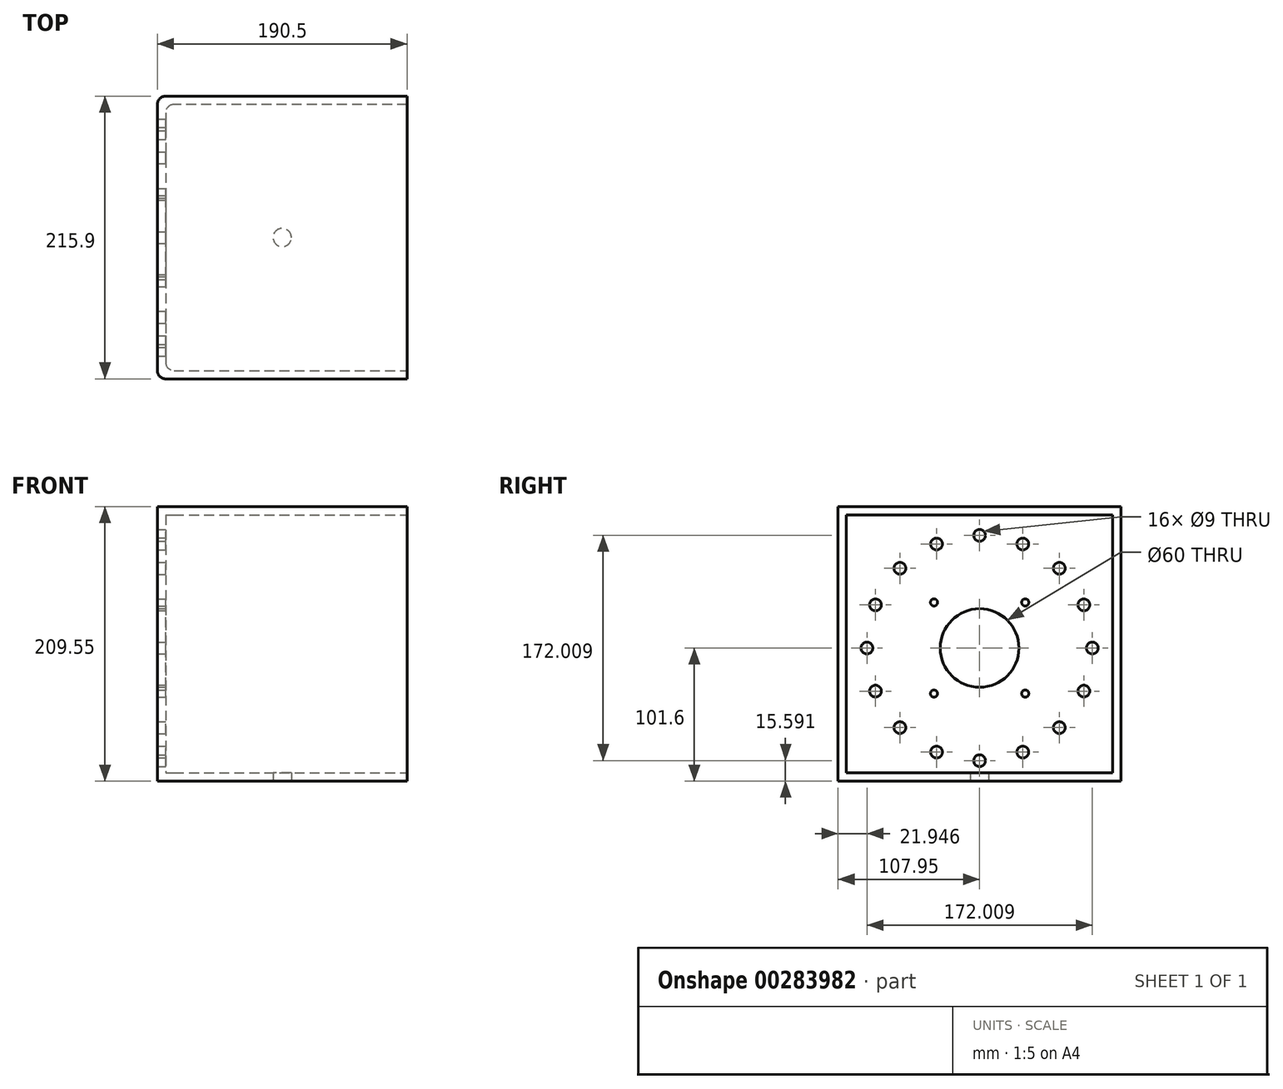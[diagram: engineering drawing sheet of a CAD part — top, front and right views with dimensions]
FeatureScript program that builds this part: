
annotation { "Feature Type Name" : "Feature", "Feature Type Description" : "" }
export const myFeature = defineFeature(function(context is Context, id is Id, definition is map)
    precondition{}
    {
        {
            var Q0;
            Q0=qCreatedBy(makeId("Top.planeOp"),FACE);
            var sketch = newSketch(context, id + "F0", { "sketchPlane" : qUnion([Q0])});
            skLineSegment(sketch, "E0.bottom", {"start": v(95.25, -107.95) * mm, "end": v(-88.9, -107.95) * mm});
            skLineSegment(sketch, "E0.top", {"start": v(95.25, 107.95) * mm, "end": v(-88.9, 107.95) * mm});
            skLineSegment(sketch, "E0.left", {"start": v(95.25, -107.95) * mm, "end": v(95.25, 107.95) * mm});
            skLineSegment(sketch, "E0.right", {"start": v(-95.25, -101.6) * mm, "end": v(-95.25, 101.6) * mm});
            skPoint(sketch, "E0.middle", {"position": v(0, 0) * mm});
            skLineSegment(sketch, "E1", {"start": v(95.25, 101.6) * mm, "end": v(-82.55, 101.6) * mm});
            skLineSegment(sketch, "E2", {"start": v(-88.9, 95.25) * mm, "end": v(-88.9, -95.25) * mm});
            skLineSegment(sketch, "E3", {"start": v(-82.55, -101.6) * mm, "end": v(95.25, -101.6) * mm});
            skPoint(sketch, "E4.visualSharp", {"position": v(-95.25, -107.95) * mm});
            skArc(sketch, "E4.filletArc", {"start": v(-95.25, -101.6) * mm, "mid": v(-93.4, -106.1) * mm, "end": v(-88.9, -107.95) * mm});
            skArc(sketch, "E5.filletArc", {"start": v(-88.9, -95.25) * mm, "mid": v(-87.04, -99.74) * mm, "end": v(-82.55, -101.6) * mm});
            skPoint(sketch, "E6.visualSharp", {"position": v(-95.25, 107.95) * mm});
            skArc(sketch, "E6.filletArc", {"start": v(-88.9, 107.95) * mm, "mid": v(-93.4, 106.1) * mm, "end": v(-95.25, 101.6) * mm});
            skArc(sketch, "E7.filletArc", {"start": v(-82.55, 101.6) * mm, "mid": v(-87.04, 99.74) * mm, "end": v(-88.9, 95.25) * mm});
            skCircle(sketch, "E8", {"center": v(0, 0) * mm, "radius": 7 * mm});
            skSolve(sketch);
        }
        {
            var Q0;
            {var subQ0=sQuery(id+"F0.wireOp",EDGE,"E1");Q0=makeQuery(id+"F0.imprint","IMPRINT",FACE,{"disambiguationData":[TD([[makeQuery(id+"F0.imprint","IMPRINT",EDGE,{"derivedFrom":subQ0}),1.0]])]});}
            extrude(context, id + "F1", {"entities" : qUnion([Q0]), "depth" : 6.35 * mm});
        }
        {
            var Q0;
            {var subQ2=sQuery(id+"F0.wireOp",EDGE,"E0.bottom");Q0=makeQuery(id+"F0.imprint","IMPRINT",FACE,{"disambiguationData":[TD([[makeQuery(id+"F0.imprint","IMPRINT",EDGE,{"derivedFrom":subQ2}),-1.0]])]});}
            extrude(context, id + "F2", {"entities" : qUnion([Q0]), "operationType" : NewBodyOperationType.ADD, "depth" : 203.2 * mm});
        }
        {
            var Q0;
            Q0=makeQuery(id+"F2.opExtrude","SWEPT_FACE",FACE,{"disambiguationData":[OSD([sQuery(id+"F0.wireOp",EDGE,"E2")])]});
            var sketch = newSketch(context, id + "F3", { "sketchPlane" : qUnion([Q0])});
            skCircle(sketch, "E9", {"center": v(0, 101.6) * mm, "radius": 30 * mm});
            skCircle(sketch, "E10", {"center": v(-34.8, 136.4) * mm, "radius": 2.75 * mm});
            skCircle(sketch, "E11.0.1.0", {"center": v(-34.8, 66.8) * mm, "radius": 2.75 * mm});
            skCircle(sketch, "E11.1.0.0", {"center": v(34.8, 136.4) * mm, "radius": 2.75 * mm});
            skCircle(sketch, "E11.1.1.0", {"center": v(34.8, 66.8) * mm, "radius": 2.75 * mm});
            skLineSegment(sketch, "E11.direction1", {"start": v(-34.8, 136.4) * mm, "end": v(34.8, 136.4) * mm, "construction": true});
            skLineSegment(sketch, "E11.direction2", {"start": v(-34.8, 136.4) * mm, "end": v(-34.8, 66.8) * mm, "construction": true});
            skCircle(sketch, "E12", {"center": v(0, 187.6) * mm, "radius": 4.5 * mm});
            skCircle(sketch, "E13.1.0", {"center": v(-32.91, 181.05) * mm, "radius": 4.5 * mm});
            skCircle(sketch, "E13.2.0", {"center": v(-60.81, 162.4) * mm, "radius": 4.5 * mm});
            skCircle(sketch, "E13.3.0", {"center": v(-79.46, 134.5) * mm, "radius": 4.5 * mm});
            skCircle(sketch, "E13.4.0", {"center": v(-86, 101.6) * mm, "radius": 4.5 * mm});
            skCircle(sketch, "E13.5.0", {"center": v(-79.46, 68.68) * mm, "radius": 4.5 * mm});
            skCircle(sketch, "E13.6.0", {"center": v(-60.81, 40.78) * mm, "radius": 4.5 * mm});
            skCircle(sketch, "E13.7.0", {"center": v(-32.91, 22.14) * mm, "radius": 4.5 * mm});
            skCircle(sketch, "E13.8.0", {"center": v(0, 15.6) * mm, "radius": 4.5 * mm});
            skCircle(sketch, "E13.9.0", {"center": v(32.91, 22.14) * mm, "radius": 4.5 * mm});
            skCircle(sketch, "E13.10.0", {"center": v(60.81, 40.78) * mm, "radius": 4.5 * mm});
            skCircle(sketch, "E13.11.0", {"center": v(79.46, 68.68) * mm, "radius": 4.5 * mm});
            skCircle(sketch, "E13.12.0", {"center": v(86, 101.6) * mm, "radius": 4.5 * mm});
            skCircle(sketch, "E13.13.0", {"center": v(79.46, 134.5) * mm, "radius": 4.5 * mm});
            skCircle(sketch, "E13.14.0", {"center": v(60.81, 162.4) * mm, "radius": 4.5 * mm});
            skCircle(sketch, "E13.15.0", {"center": v(32.91, 181.05) * mm, "radius": 4.5 * mm});
            skSolve(sketch);
        }
        {
            var Q0;
            Q0=makeQuery(id+"F3.imprint","IMPRINT",FACE,{"disambiguationData":[TD([[makeQuery(id+"F3.imprint","IMPRINT",EDGE,{"derivedFrom":sQuery(id+"F3.wireOp",EDGE,"E13.10.0")}),1.0]])]});
            var Q1;
            Q1=makeQuery(id+"F3.imprint","IMPRINT",FACE,{"disambiguationData":[TD([[makeQuery(id+"F3.imprint","IMPRINT",EDGE,{"derivedFrom":sQuery(id+"F3.wireOp",EDGE,"E13.9.0")}),1.0]])]});
            var Q2;
            Q2=makeQuery(id+"F3.imprint","IMPRINT",FACE,{"disambiguationData":[TD([[makeQuery(id+"F3.imprint","IMPRINT",EDGE,{"derivedFrom":sQuery(id+"F3.wireOp",EDGE,"E13.8.0")}),1.0]])]});
            var Q3;
            Q3=makeQuery(id+"F3.imprint","IMPRINT",FACE,{"disambiguationData":[TD([[makeQuery(id+"F3.imprint","IMPRINT",EDGE,{"derivedFrom":sQuery(id+"F3.wireOp",EDGE,"E13.7.0")}),1.0]])]});
            var Q4;
            Q4=makeQuery(id+"F3.imprint","IMPRINT",FACE,{"disambiguationData":[TD([[makeQuery(id+"F3.imprint","IMPRINT",EDGE,{"derivedFrom":sQuery(id+"F3.wireOp",EDGE,"E13.5.0")}),1.0]])]});
            var Q5;
            Q5=makeQuery(id+"F3.imprint","IMPRINT",FACE,{"disambiguationData":[TD([[makeQuery(id+"F3.imprint","IMPRINT",EDGE,{"derivedFrom":sQuery(id+"F3.wireOp",EDGE,"E13.4.0")}),1.0]])]});
            var Q6;
            Q6=makeQuery(id+"F3.imprint","IMPRINT",FACE,{"disambiguationData":[TD([[makeQuery(id+"F3.imprint","IMPRINT",EDGE,{"derivedFrom":sQuery(id+"F3.wireOp",EDGE,"E13.3.0")}),1.0]])]});
            var Q7;
            Q7=makeQuery(id+"F3.imprint","IMPRINT",FACE,{"disambiguationData":[TD([[makeQuery(id+"F3.imprint","IMPRINT",EDGE,{"derivedFrom":sQuery(id+"F3.wireOp",EDGE,"E13.2.0")}),1.0]])]});
            var Q8;
            Q8=makeQuery(id+"F3.imprint","IMPRINT",FACE,{"disambiguationData":[TD([[makeQuery(id+"F3.imprint","IMPRINT",EDGE,{"derivedFrom":sQuery(id+"F3.wireOp",EDGE,"E13.1.0")}),1.0]])]});
            var Q9;
            Q9=makeQuery(id+"F3.imprint","IMPRINT",FACE,{"disambiguationData":[TD([[makeQuery(id+"F3.imprint","IMPRINT",EDGE,{"derivedFrom":sQuery(id+"F3.wireOp",EDGE,"E12")}),1.0]])]});
            var Q10;
            Q10=makeQuery(id+"F3.imprint","IMPRINT",FACE,{"disambiguationData":[TD([[makeQuery(id+"F3.imprint","IMPRINT",EDGE,{"derivedFrom":sQuery(id+"F3.wireOp",EDGE,"E13.15.0")}),1.0]])]});
            var Q11;
            Q11=makeQuery(id+"F3.imprint","IMPRINT",FACE,{"disambiguationData":[TD([[makeQuery(id+"F3.imprint","IMPRINT",EDGE,{"derivedFrom":sQuery(id+"F3.wireOp",EDGE,"E13.14.0")}),1.0]])]});
            var Q12;
            Q12=makeQuery(id+"F3.imprint","IMPRINT",FACE,{"disambiguationData":[TD([[makeQuery(id+"F3.imprint","IMPRINT",EDGE,{"derivedFrom":sQuery(id+"F3.wireOp",EDGE,"E13.13.0")}),1.0]])]});
            var Q13;
            Q13=makeQuery(id+"F3.imprint","IMPRINT",FACE,{"disambiguationData":[TD([[makeQuery(id+"F3.imprint","IMPRINT",EDGE,{"derivedFrom":sQuery(id+"F3.wireOp",EDGE,"E13.12.0")}),1.0]])]});
            var Q14;
            Q14=makeQuery(id+"F3.imprint","IMPRINT",FACE,{"disambiguationData":[TD([[makeQuery(id+"F3.imprint","IMPRINT",EDGE,{"derivedFrom":sQuery(id+"F3.wireOp",EDGE,"E13.11.0")}),1.0]])]});
            extrude(context, id + "F4", {"entities" : qUnion([Q0, Q1, Q2, Q3, Q4, Q5, Q6, Q7, Q8, Q9, Q10, Q11, Q12, Q13, Q14]), "operationType" : NewBodyOperationType.REMOVE, "endBound" : BoundingType.THROUGH_ALL, "oppositeDirection" : true, "depth" : 25.4 * mm});
        }
        {
            var Q0;
            Q0=makeQuery(id+"F3.imprint","IMPRINT",FACE,{"disambiguationData":[TD([[makeQuery(id+"F3.imprint","IMPRINT",EDGE,{"derivedFrom":sQuery(id+"F3.wireOp",EDGE,"E13.6.0")}),1.0]])]});
            var Q1;
            Q1=makeQuery(id+"F3.imprint","IMPRINT",FACE,{"disambiguationData":[TD([[makeQuery(id+"F3.imprint","IMPRINT",EDGE,{"derivedFrom":sQuery(id+"F3.wireOp",EDGE,"E11.0.1.0")}),1.0]])]});
            var Q2;
            Q2=makeQuery(id+"F3.imprint","IMPRINT",FACE,{"disambiguationData":[TD([[makeQuery(id+"F3.imprint","IMPRINT",EDGE,{"derivedFrom":sQuery(id+"F3.wireOp",EDGE,"E11.1.1.0")}),1.0]])]});
            var Q3;
            Q3=makeQuery(id+"F3.imprint","IMPRINT",FACE,{"disambiguationData":[TD([[makeQuery(id+"F3.imprint","IMPRINT",EDGE,{"derivedFrom":sQuery(id+"F3.wireOp",EDGE,"E11.1.0.0")}),1.0]])]});
            var Q4;
            Q4=makeQuery(id+"F3.imprint","IMPRINT",FACE,{"disambiguationData":[TD([[makeQuery(id+"F3.imprint","IMPRINT",EDGE,{"derivedFrom":sQuery(id+"F3.wireOp",EDGE,"E10")}),1.0]])]});
            var Q5;
            Q5=makeQuery(id+"F3.imprint","IMPRINT",FACE,{"disambiguationData":[TD([[makeQuery(id+"F3.imprint","IMPRINT",EDGE,{"derivedFrom":sQuery(id+"F3.wireOp",EDGE,"E9")}),1.0]])]});
            extrude(context, id + "F5", {"entities" : qUnion([Q0, Q1, Q2, Q3, Q4, Q5]), "operationType" : NewBodyOperationType.REMOVE, "endBound" : BoundingType.THROUGH_ALL, "oppositeDirection" : true, "depth" : 25.4 * mm});
        }
        {
            var Q0;
            Q0=makeQuery(id+"F2.opExtrude","CAP_FACE",FACE,{"disambiguationData":[OSD([sQuery(id+"F0.wireOp",EDGE,"E0.bottom"),sQuery(id+"F0.wireOp",EDGE,"E0.top"),sQuery(id+"F0.wireOp",EDGE,"E0.left"),sQuery(id+"F0.wireOp",EDGE,"E0.right"),sQuery(id+"F0.wireOp",EDGE,"E1"),sQuery(id+"F0.wireOp",EDGE,"E2"),sQuery(id+"F0.wireOp",EDGE,"E3"),sQuery(id+"F0.wireOp",EDGE,"E4.filletArc"),sQuery(id+"F0.wireOp",EDGE,"E5.filletArc"),sQuery(id+"F0.wireOp",EDGE,"E6.filletArc"),sQuery(id+"F0.wireOp",EDGE,"E7.filletArc")])],"isStart":false});
            var sketch = newSketch(context, id + "F6", { "sketchPlane" : qUnion([Q0])});
            skLineSegment(sketch, "E14.bottom", {"start": v(-88.9, 107.95) * mm, "end": v(95.25, 107.95) * mm});
            skLineSegment(sketch, "E14.top", {"start": v(-88.9, -107.95) * mm, "end": v(95.25, -107.95) * mm});
            skLineSegment(sketch, "E14.left", {"start": v(-95.25, 101.6) * mm, "end": v(-95.25, -101.6) * mm});
            skLineSegment(sketch, "E14.right", {"start": v(95.25, 107.95) * mm, "end": v(95.25, -107.95) * mm});
            skPoint(sketch, "E14.middle", {"position": v(0, 0) * mm});
            skPoint(sketch, "E15.visualSharp", {"position": v(-95.25, 107.95) * mm});
            skArc(sketch, "E15.filletArc", {"start": v(-88.9, 107.95) * mm, "mid": v(-93.4, 106.1) * mm, "end": v(-95.25, 101.6) * mm});
            skPoint(sketch, "E16.visualSharp", {"position": v(-95.25, -107.95) * mm});
            skArc(sketch, "E16.filletArc", {"start": v(-95.25, -101.6) * mm, "mid": v(-93.4, -106.1) * mm, "end": v(-88.9, -107.95) * mm});
            skSolve(sketch);
        }
        {
            var Q0;
            {var subQ1=makeQuery(id+"F2.opExtrude","CAP_EDGE",EDGE,{"disambiguationData":[OSD([sQuery(id+"F0.wireOp",EDGE,"E1")])],"isStart":false});Q0=makeQuery(id+"F6.imprint","IMPRINT",FACE,{"disambiguationData":[TD([[makeQuery(id+"F6.imprint","IMPRINT",EDGE,{"derivedFrom":subQ1}),1.0]])]});}
            var Q1;
            {var subQ3=sQuery(id+"F6.wireOp",EDGE,"E14.bottom");Q1=makeQuery(id+"F6.imprint","IMPRINT",FACE,{"disambiguationData":[TD([[makeQuery(id+"F6.imprint","IMPRINT",EDGE,{"derivedFrom":subQ3}),1.0]])]});}
            extrude(context, id + "F7", {"entities" : qUnion([Q0, Q1]), "operationType" : NewBodyOperationType.ADD, "depth" : 6.35 * mm});
        }
    });
